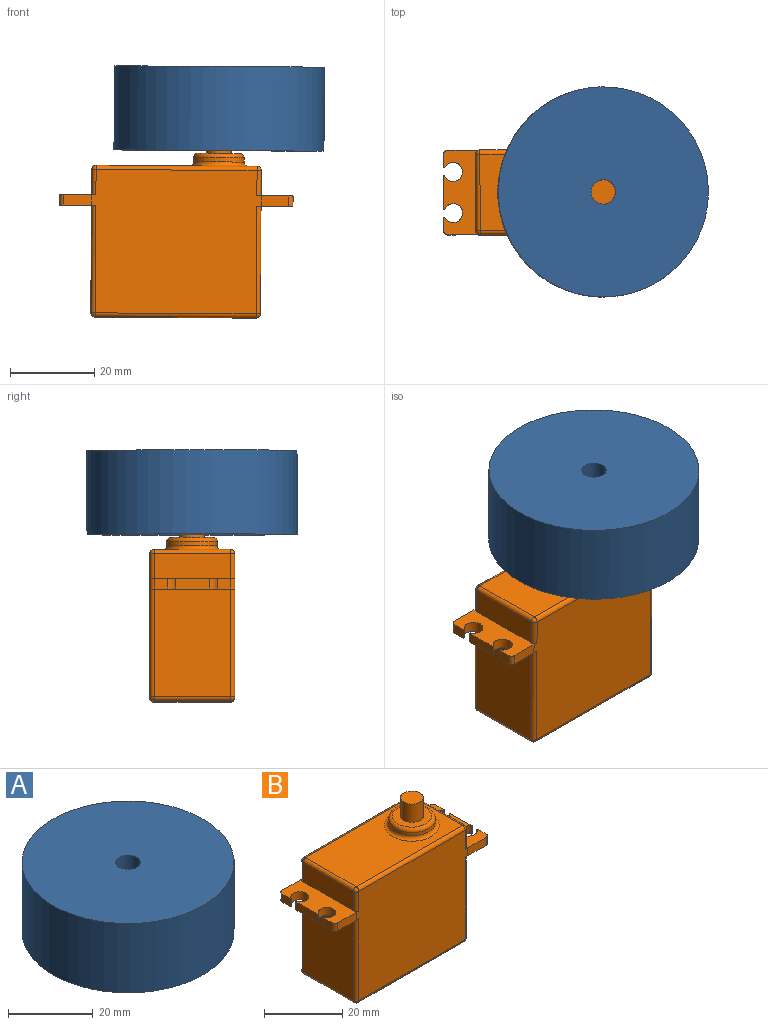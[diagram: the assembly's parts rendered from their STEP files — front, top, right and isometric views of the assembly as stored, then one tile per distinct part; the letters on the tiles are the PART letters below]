
ASSEMBLY  parts=2 mates=1
PART A: 4 faces, bbox 50x50x20 mm
  f0: cylinder r=2.9mm len=20mm, axis (0,0,-1), area 364.4mm2, adj f2,f3
  f1: cylinder r=25mm len=50mm, axis (0,0,-1), area 3141.6mm2, adj f2,f3
  f2: plane 50x50mm, normal (0,0,1), area 1937.1mm2, adj f0,f1
  f3: plane 50x50mm, normal (0,0,-1), area 1937.1mm2, adj f0,f1
PART B: 68 faces, bbox 55.5x20.2x44.8 mm
  f0: plane 7.99x2.5mm, normal (1,0,0), area 20mm2, adj f1,f2,f12,f21
  f1: plane 20.2x8.6mm, normal (0,0,1), area 121.4mm2, adj f0,f6,f7,f8,f9,f10,f11,f12
  f2: plane 20.2x8.6mm, normal (0,0,-1), area 121.4mm2, adj f0,f3,f7,f8,f9,f10,f11,f12
  f3: plane 25.6x18.2mm, normal (1,0,0), area 465.9mm2, adj f2,f13,f22,f62
  f4: plane 38.3x18.2mm, normal (0,0,1), area 543.1mm2, adj f50,f52,f55,f56,f59
  f5: plane 38.3x18.2mm, normal (0,0,-1), area 697.1mm2, adj f61,f62,f65,f66
  f6: plane 18.2x6mm, normal (1,0,0), area 109.2mm2, adj f1,f15,f24,f56
  f7: plane 40.3x34.1mm, normal (0,-1,0), area 1311mm2, adj f1,f2,f9,f13,f15,f26,f27,f31
  f8: plane 3.11x2.5mm, normal (1,0,0), area 7.8mm2, adj f1,f2,f10,f14
  f9: plane 6.6x2.5mm, normal (0,-1,0), area 16.5mm2, adj f1,f2,f7,f14
  f10: plane 2.5x0.28mm, normal (0,1,0), area 0.7mm2, adj f1,f2,f8,f11
  f11: cylinder r=2.25mm len=4.5mm, axis (0,0,-1), area 30.2mm2, adj f1,f2,f10,f12
  f12: plane 2.5x0.19mm, normal (0,-1,0), area 0.5mm2, adj f0,f1,f2,f11
  f13: cylinder r=1mm len=25.6mm, axis (0,0,-1), area 40.2mm2, adj f2,f3,f7,f60
  f14: cylinder r=1mm len=2.5mm, axis (0,0,1), area 3.9mm2, adj f1,f2,f8,f9
  f15: cylinder r=1mm len=6mm, axis (0,0,-1), area 9.4mm2, adj f1,f6,f7,f58
  f16: plane 40.3x34.1mm, normal (0,1,0), area 1311mm2, adj f1,f2,f18,f22,f24,f26,f27,f39
  f17: plane 3.11x2.5mm, normal (1,0,0), area 7.8mm2, adj f1,f2,f19,f23
  f18: plane 6.6x2.5mm, normal (0,1,0), area 16.5mm2, adj f1,f2,f16,f23
  f19: plane 2.5x0.28mm, normal (0,-1,0), area 0.7mm2, adj f1,f2,f17,f20
  f20: cylinder r=2.25mm len=4.5mm, axis (0,0,-1), area 30.2mm2, adj f1,f2,f19,f21
  f21: plane 2.5x0.19mm, normal (0,1,0), area 0.5mm2, adj f0,f1,f2,f20
  f22: cylinder r=1mm len=25.6mm, axis (0,0,-1), area 40.2mm2, adj f2,f3,f16,f64
  f23: cylinder r=1mm len=2.5mm, axis (0,0,1), area 3.9mm2, adj f1,f2,f17,f18
  f24: cylinder r=1mm len=6mm, axis (0,0,-1), area 9.4mm2, adj f1,f6,f16,f54
  f25: plane 7.99x2.5mm, normal (-1,0,0), area 20mm2, adj f26,f27,f34,f42
  f26: plane 20.2x8.6mm, normal (0,0,1), area 121.4mm2, adj f7,f16,f25,f29,f30,f31,f32,f33
  f27: plane 20.2x8.6mm, normal (0,0,-1), area 121.4mm2, adj f7,f16,f25,f28,f30,f31,f32,f33
  f28: plane 25.6x18.2mm, normal (-1,0,0), area 465.9mm2, adj f27,f35,f43,f65
  f29: plane 18.2x6mm, normal (-1,0,0), area 109.2mm2, adj f26,f37,f45,f55
  f30: plane 3.11x2.5mm, normal (-1,0,0), area 7.8mm2, adj f26,f27,f32,f36
  f31: plane 6.6x2.5mm, normal (0,-1,0), area 16.5mm2, adj f7,f26,f27,f36
  f32: plane 2.5x0.28mm, normal (0,1,0), area 0.7mm2, adj f26,f27,f30,f33
  f33: cylinder r=2.25mm len=4.5mm, axis (0,0,-1), area 30.2mm2, adj f26,f27,f32,f34
  f34: plane 2.5x0.19mm, normal (0,-1,0), area 0.5mm2, adj f25,f26,f27,f33
  f35: cylinder r=1mm len=25.6mm, axis (0,0,-1), area 40.2mm2, adj f7,f27,f28,f63
  f36: cylinder r=1mm len=2.5mm, axis (0,0,1), area 3.9mm2, adj f26,f27,f30,f31
  f37: cylinder r=1mm len=6mm, axis (0,0,-1), area 9.4mm2, adj f7,f26,f29,f57
  f38: plane 3.11x2.5mm, normal (-1,0,0), area 7.8mm2, adj f26,f27,f40,f44
  f39: plane 6.6x2.5mm, normal (0,1,0), area 16.5mm2, adj f16,f26,f27,f44
  f40: plane 2.5x0.28mm, normal (0,-1,0), area 0.7mm2, adj f26,f27,f38,f41
  f41: cylinder r=2.25mm len=4.5mm, axis (0,0,-1), area 30.2mm2, adj f26,f27,f40,f42
  f42: plane 2.5x0.19mm, normal (0,1,0), area 0.5mm2, adj f25,f26,f27,f41
  f43: cylinder r=1mm len=25.6mm, axis (0,0,-1), area 40.2mm2, adj f16,f27,f28,f67
  f44: cylinder r=1mm len=2.5mm, axis (0,0,1), area 3.9mm2, adj f26,f27,f38,f39
  f45: cylinder r=1mm len=6mm, axis (0,0,-1), area 9.4mm2, adj f16,f26,f29,f53
  f46: cylinder r=6mm len=12mm, axis (0,0,-1), area 37.7mm2, adj f50,f51
  f47: plane 10x10mm, normal (0,0,1), area 52.1mm2, adj f49,f51
  f48: plane 5.8x5.8mm, normal (0,0,1), area 26.4mm2, adj f49
  f49: cylinder r=2.9mm len=5.8mm, axis (0,0,-1), area 103.9mm2, adj f47,f48
  f50: torus R=7mm, axis (0,0,1), area 62.8mm2, adj f4,f46
  f51: torus R=5mm, axis (0,0,1), area 55.6mm2, adj f46,f47
  f52: cylinder r=1mm len=38.3mm, axis (1,0,0), area 60.2mm2, adj f4,f16,f53,f54
  f53: sphere r=1mm, area 1.6mm2, adj f45,f52,f55
  f54: sphere r=1mm, area 1.6mm2, adj f24,f52,f56
  f55: cylinder r=1mm len=18.2mm, axis (0,1,0), area 28.6mm2, adj f4,f29,f53,f57
  f56: cylinder r=1mm len=18.2mm, axis (0,1,0), area 28.6mm2, adj f4,f6,f54,f58
  f57: sphere r=1mm, area 1.6mm2, adj f37,f55,f59
  f58: sphere r=1mm, area 1.6mm2, adj f15,f56,f59
  f59: cylinder r=1mm len=38.3mm, axis (1,0,0), area 60.2mm2, adj f4,f7,f57,f58
  f60: sphere r=1mm, area 1.6mm2, adj f13,f61,f62
  f61: cylinder r=1mm len=38.3mm, axis (-1,0,0), area 60.2mm2, adj f5,f7,f60,f63
  f62: cylinder r=1mm len=18.2mm, axis (0,-1,0), area 28.6mm2, adj f3,f5,f60,f64
  f63: sphere r=1mm, area 1.6mm2, adj f35,f61,f65
  f64: sphere r=1mm, area 1.6mm2, adj f22,f62,f66
  f65: cylinder r=1mm len=18.2mm, axis (0,-1,0), area 28.6mm2, adj f5,f28,f63,f67
  f66: cylinder r=1mm len=38.3mm, axis (-1,0,0), area 60.2mm2, adj f5,f16,f64,f67
  f67: sphere r=1mm, area 1.6mm2, adj f43,f65,f66
PLACE A rot(axis=(-0.13,0.94,0.3),0.4deg) t=(-8.05,6.95,-10.46)mm
PLACE B rot(axis=(-0.13,0.94,0.3),0.4deg) t=(3.88,17.05,-39.67)mm
MATE pin_slot B.f50 <-> A.f0  axis (0.01,0,1) through (-8.02,6.95,-5.46)mm
